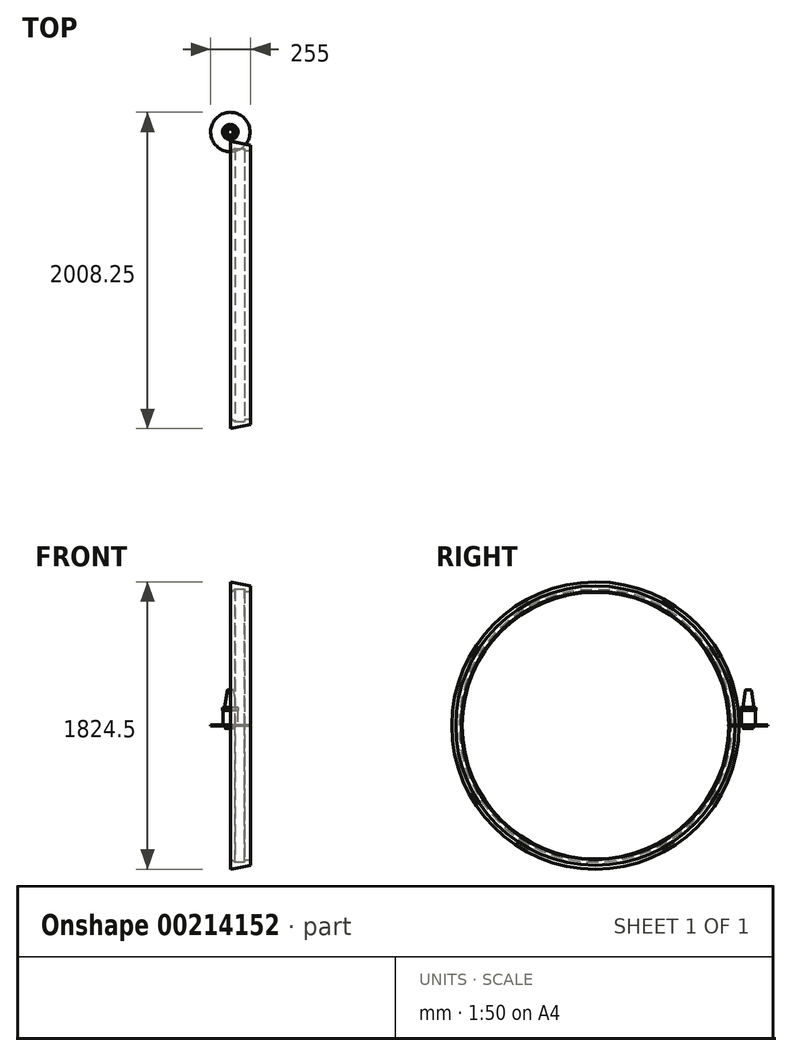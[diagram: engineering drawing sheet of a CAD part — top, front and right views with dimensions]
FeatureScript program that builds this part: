
annotation { "Feature Type Name" : "Feature", "Feature Type Description" : "" }
export const myFeature = defineFeature(function(context is Context, id is Id, definition is map)
    precondition{}
    {
        {
            var Q0;
            Q0=qCreatedBy(makeId("Front.planeOp"),FACE);
            var sketch = newSketch(context, id + "F0", { "sketchPlane" : qUnion([Q0])});
            skLineSegment(sketch, "E0", {"start": v(0, 852) * mm, "end": v(-40, 852) * mm});
            skLineSegment(sketch, "E1", {"start": v(-40, 852) * mm, "end": v(-40, 867) * mm});
            skLineSegment(sketch, "E2", {"start": v(-100, 867) * mm, "end": v(-40, 867) * mm});
            skLineSegment(sketch, "E3", {"start": v(-100, 867) * mm, "end": v(-130, 847) * mm});
            skLineSegment(sketch, "E4", {"start": v(-130, 847) * mm, "end": v(-130, 912.25) * mm});
            skLineSegment(sketch, "E5", {"start": v(-130, 912.25) * mm, "end": v(0, 887) * mm});
            skLineSegment(sketch, "E6", {"start": v(0, 887) * mm, "end": v(0, 852) * mm});
            skLineSegment(sketch, "E7", {"start": v(0, 0) * mm, "end": v(-563.15, 0) * mm, "construction": true});
            skSolve(sketch);
        }
        {
            var Q0;
            Q0 = qSketchRegion(id + "F0", true);
            var Q1;
            Q1=sQuery(id+"F0.wireOp",EDGE,"E7");
            revolve(context, id + "F1", {"entities" : qUnion([Q0]), "axis" : qUnion([Q1]), "revolveType" : RevolveType.FULL});
        }
        {
            var Q0;
            Q0=qCreatedBy(makeId("Right.planeOp"),FACE);
            var sketch = newSketch(context, id + "F2", { "sketchPlane" : qUnion([Q0])});
            skLineSegment(sketch, "E8", {"start": v(0, 0) * mm, "end": v(919.15, 0) * mm, "construction": true});
            skLineSegment(sketch, "E9", {"start": v(919.15, 0) * mm, "end": v(919.15, -3) * mm});
            skLineSegment(sketch, "E10", {"start": v(567.02, -3) * mm, "end": v(919.15, -3) * mm});
            skLineSegment(sketch, "E11.MirrorCS", {"start": v(567.02, 3) * mm, "end": v(919.15, 3) * mm});
            skLineSegment(sketch, "E12.MirrorCS", {"start": v(919.15, 0) * mm, "end": v(919.15, 3) * mm});
            skLineSegment(sketch, "E13", {"start": v(567.02, 3) * mm, "end": v(567.02, -3) * mm});
            skSolve(sketch);
        }
        {
            var Q0;
            Q0=makeQuery(id+"F2.imprint","IMPRINT",FACE,{"disambiguationData":[TD([[makeQuery(id+"F2.imprint","IMPRINT",EDGE,{"derivedFrom":sQuery(id+"F2.wireOp",EDGE,"E9")}),-1.0]])]});
            var Q1;
            Q1 = qConstructionFilter(qBodyType(qCreatedBy(id + "F2" ,EDGE), BodyType.WIRE), ConstructionObject.NO);
            extrude(context, id + "F3", {"entities" : qUnion([Q0]), "operationType" : NewBodyOperationType.REMOVE, "surfaceEntities" : qUnion([Q1]), "oppositeDirection" : true, "depth" : 130 * mm});
        }
        {
            var Q0;
            Q0=qCreatedBy(makeId("Top.planeOp"),FACE);
            var sketch = newSketch(context, id + "F4", { "sketchPlane" : qUnion([Q0])});
            skCircle(sketch, "E14", {"center": v(-130, 971) * mm, "radius": 125 * mm});
            skSolve(sketch);
        }
        {
            var Q0;
            Q0 = qSketchRegion(id + "F4", true);
            extrude(context, id + "F5", {"entities" : qUnion([Q0]), "operationType" : NewBodyOperationType.ADD, "oppositeDirection" : true, "depth" : 3 * mm, "hasSecondDirection" : true, "secondDirectionOppositeDirection" : false, "secondDirectionDepth" : 3 * mm});
        }
        {
            var Q0;
            Q0=makeQuery(id+"F5.opExtrude","CAP_FACE",FACE,{"disambiguationData":[OSD([sQuery(id+"F4.wireOp",EDGE,"E14")])],"isStart":true});
            var sketch = newSketch(context, id + "F6", { "sketchPlane" : qUnion([Q0])});
            skCircle(sketch, "E15", {"center": v(-130, 971) * mm, "radius": 35.5 * mm});
            skSolve(sketch);
        }
        {
            var Q0;
            Q0 = qSketchRegion(id + "F6", true);
            extrude(context, id + "F7", {"entities" : qUnion([Q0]), "operationType" : NewBodyOperationType.ADD, "depth" : 3 * mm});
        }
        {
            var Q0;
            Q0=makeQuery(id+"F5.opExtrude","CAP_FACE",FACE,{"disambiguationData":[OSD([sQuery(id+"F4.wireOp",EDGE,"E14")])],"isStart":false});
            var sketch = newSketch(context, id + "F8", { "sketchPlane" : qUnion([Q0])});
            skCircle(sketch, "E16", {"center": v(-130, -971) * mm, "radius": 35.5 * mm});
            skSolve(sketch);
        }
        {
            var Q0;
            Q0=makeQuery(id+"F8.imprint","IMPRINT",FACE,{"disambiguationData":[TD([[makeQuery(id+"F8.imprint","IMPRINT",EDGE,{"derivedFrom":sQuery(id+"F8.wireOp",EDGE,"E16")}),1.0]])]});
            extrude(context, id + "F9", {"entities" : qUnion([Q0]), "operationType" : NewBodyOperationType.ADD, "depth" : 3 * mm});
        }
        {
            var Q0;
            Q0=makeQuery(id+"F7.opExtrude","CAP_FACE",FACE,{"disambiguationData":[OSD([sQuery(id+"F6.wireOp",EDGE,"E15")])],"isStart":false});
            var sketch = newSketch(context, id + "F10", { "sketchPlane" : qUnion([Q0])});
            skCircle(sketch, "E17", {"center": v(-130, 971) * mm, "radius": 45 * mm});
            skSolve(sketch);
        }
        {
            var Q0;
            Q0 = qSketchRegion(id + "F10", true);
            extrude(context, id + "F11", {"entities" : qUnion([Q0]), "operationType" : NewBodyOperationType.ADD, "depth" : (110 - 19) * mm});
        }
        {
            var Q0;
            Q0=makeQuery(id+"F11.opExtrude","CAP_FACE",FACE,{"disambiguationData":[OSD([sQuery(id+"F10.wireOp",EDGE,"E17")])],"isStart":false});
            var sketch = newSketch(context, id + "F12", { "sketchPlane" : qUnion([Q0])});
            skCircle(sketch, "E18", {"center": v(-130, 971) * mm, "radius": 48.75 * mm});
            skSolve(sketch);
        }
        {
            var Q0;
            Q0 = qSketchRegion(id + "F12", true);
            extrude(context, id + "F13", {"entities" : qUnion([Q0]), "operationType" : NewBodyOperationType.ADD, "depth" : 19 * mm});
        }
        {
            var Q0;
            Q0=makeQuery(id+"F13.opExtrude","CAP_FACE",FACE,{"disambiguationData":[OSD([sQuery(id+"F12.wireOp",EDGE,"E18")])],"isStart":false});
            var sketch = newSketch(context, id + "F14", { "sketchPlane" : qUnion([Q0])});
            skCircle(sketch, "E19", {"center": v(-130, 971) * mm, "radius": 35 * mm});
            skSolve(sketch);
        }
        {
            var Q0;
            Q0=makeQuery(id+"F14.imprint","IMPRINT",FACE,{"disambiguationData":[TD([[makeQuery(id+"F14.imprint","IMPRINT",EDGE,{"derivedFrom":sQuery(id+"F14.wireOp",EDGE,"E19")}),1.0]])]});
            extrude(context, id + "F15", {"entities" : qUnion([Q0]), "operationType" : NewBodyOperationType.ADD, "depth" : 110 * mm, "hasDraft" : true, "draftAngle" : 8.29 * degree, "draftPullDirection" : true});
        }
        {
            var Q0;
            Q0=makeQuery(id+"F9.opExtrude","CAP_FACE",FACE,{"disambiguationData":[OSD([sQuery(id+"F8.wireOp",EDGE,"E16")])],"isStart":false});
            var sketch = newSketch(context, id + "F16", { "sketchPlane" : qUnion([Q0])});
            skArc(sketch, "E20", {"start": v(-120, -941.13) * mm, "mid": v(-130, -939.5) * mm, "end": v(-140, -941.13) * mm});
            skLineSegment(sketch, "E21", {"start": v(-130, -971) * mm, "end": v(-120, -971) * mm, "construction": true});
            skLineSegment(sketch, "E22", {"start": v(-120, -971) * mm, "end": v(-120, -961) * mm, "construction": true});
            skLineSegment(sketch, "E23", {"start": v(-120, -961) * mm, "end": v(-120, -941.13) * mm});
            skLineSegment(sketch, "E24", {"start": v(-120, -961) * mm, "end": v(-100.13, -961) * mm});
            skLineSegment(sketch, "E25.1.0", {"start": v(892.25, 376.58) * mm, "end": v(863.44, 359.94) * mm});
            skLineSegment(sketch, "E25.1.1", {"start": v(900.91, 381.58) * mm, "end": v(892.25, 376.58) * mm, "construction": true});
            skLineSegment(sketch, "E25.1.2", {"start": v(892.25, 376.58) * mm, "end": v(874.88, 406.67) * mm});
            skLineSegment(sketch, "E25.1.3", {"start": v(905.91, 372.92) * mm, "end": v(900.91, 381.58) * mm, "construction": true});
            skLineSegment(sketch, "E25.2.0", {"start": v(-772.25, 584.42) * mm, "end": v(-743.44, 567.79) * mm});
            skLineSegment(sketch, "E25.2.1", {"start": v(-780.91, 589.42) * mm, "end": v(-772.25, 584.42) * mm, "construction": true});
            skLineSegment(sketch, "E25.2.2", {"start": v(-772.25, 584.42) * mm, "end": v(-789.62, 554.33) * mm});
            skLineSegment(sketch, "E25.2.3", {"start": v(-775.91, 598.08) * mm, "end": v(-780.91, 589.42) * mm, "construction": true});
            skPoint(sketch, "E25.center", {"position": v(0, 0) * mm});
            skLineSegment(sketch, "E26.MirrorCS", {"start": v(-120, -981) * mm, "end": v(-100.13, -981) * mm});
            skLineSegment(sketch, "E27.MirrorCS", {"start": v(-120, -981) * mm, "end": v(-120, -1014.27) * mm});
            skLineSegment(sketch, "E28", {"start": v(-130, -971) * mm, "end": v(-130, -982.59) * mm, "construction": true});
            skLineSegment(sketch, "E29.MirrorCS", {"start": v(-140, -981) * mm, "end": v(-140, -1000.87) * mm});
            skLineSegment(sketch, "E30.MirrorCS", {"start": v(-140, -981) * mm, "end": v(-159.87, -981) * mm});
            skLineSegment(sketch, "E31.MirrorCS", {"start": v(-140, -961) * mm, "end": v(-159.87, -961) * mm});
            skPoint(sketch, "E32.orphan", {"position": v(-120, -927.73) * mm});
            skArc(sketch, "E33.trimOffspring", {"start": v(-100.13, -981) * mm, "mid": v(-98.5, -971) * mm, "end": v(-100.13, -961) * mm});
            skPoint(sketch, "E34.orphan", {"position": v(-85.26, -981) * mm});
            skPoint(sketch, "E35.orphan", {"position": v(-85.26, -961) * mm});
            skPoint(sketch, "E36.orphan", {"position": v(-140, -927.73) * mm});
            skPoint(sketch, "E37.MirrorCS.start.orphan", {"position": v(-140, -961) * mm});
            skLineSegment(sketch, "E38", {"start": v(-140, -961) * mm, "end": v(-140, -941.13) * mm});
            skArc(sketch, "E39.trimOffspring", {"start": v(-159.87, -961) * mm, "mid": v(-161.5, -971) * mm, "end": v(-159.87, -981) * mm});
            skPoint(sketch, "E40.orphan", {"position": v(-174.74, -961) * mm});
            skArc(sketch, "E41.trimOffspring", {"start": v(-140, -1000.87) * mm, "mid": v(-130, -1002.5) * mm, "end": v(-120, -1000.87) * mm});
            skPoint(sketch, "E42.orphan", {"position": v(-140, -1014.27) * mm});
            skPoint(sketch, "E43.orphan", {"position": v(-174.74, -981) * mm});
            skSolve(sketch);
        }
        {
            var Q0;
            Q0=makeQuery(id+"F16.imprint","IMPRINT",FACE,{"disambiguationData":[TD([[makeQuery(id+"F16.imprint","IMPRINT",EDGE,{"derivedFrom":sQuery(id+"F16.wireOp",EDGE,"E20")}),1.0]])]});
            extrude(context, id + "F17", {"entities" : qUnion([Q0]), "operationType" : NewBodyOperationType.ADD, "depth" : 12 * mm});
        }
    });
